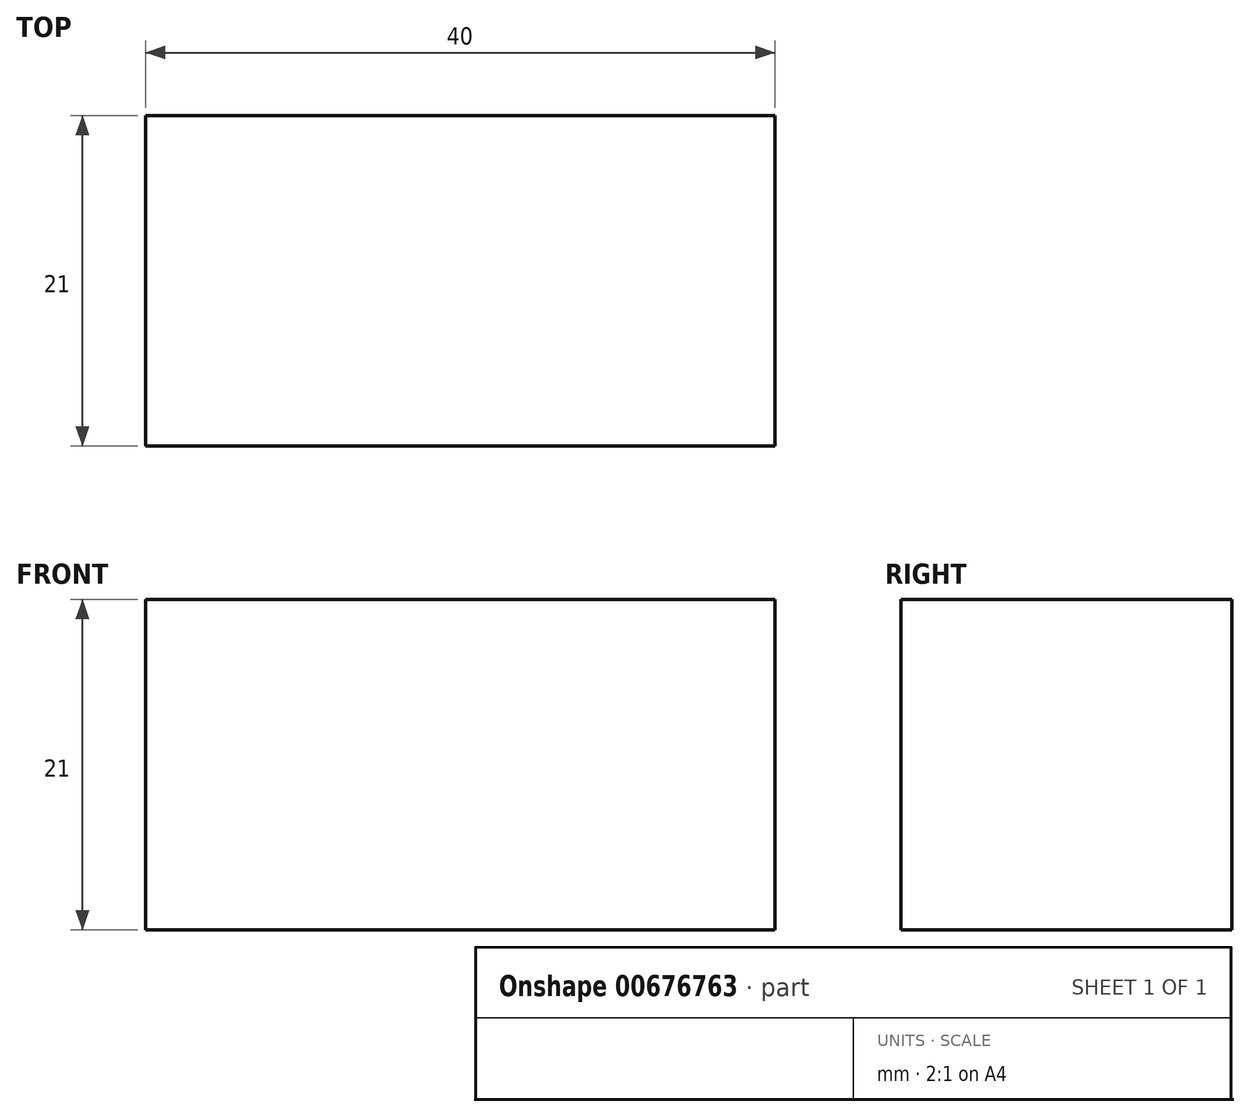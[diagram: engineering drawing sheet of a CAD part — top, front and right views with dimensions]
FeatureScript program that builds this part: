
annotation { "Feature Type Name" : "Feature", "Feature Type Description" : "" }
export const myFeature = defineFeature(function(context is Context, id is Id, definition is map)
    precondition{}
    {
        {
            var Q0;
            Q0=qCreatedBy(makeId("Right.planeOp"),FACE);
            var sketch = newSketch(context, id + "F0", { "sketchPlane" : qUnion([Q0])});
            skLineSegment(sketch, "E0.bottom", {"start": v(10.5, -10.5) * mm, "end": v(-10.5, -10.5) * mm});
            skLineSegment(sketch, "E0.top", {"start": v(10.5, 10.5) * mm, "end": v(-10.5, 10.5) * mm});
            skLineSegment(sketch, "E0.left", {"start": v(10.5, -10.5) * mm, "end": v(10.5, 10.5) * mm});
            skLineSegment(sketch, "E0.right", {"start": v(-10.5, -10.5) * mm, "end": v(-10.5, 10.5) * mm});
            skPoint(sketch, "E0.middle", {"position": v(0, 0) * mm});
            skSolve(sketch);
        }
        {
            var Q0;
            Q0=makeQuery(id+"F0.imprint","IMPRINT",FACE,{"disambiguationData":[TD([[makeQuery(id+"F0.imprint","IMPRINT",EDGE,{"derivedFrom":sQuery(id+"F0.wireOp",EDGE,"E0.bottom")}),-1.0]])]});
            extrude(context, id + "F1", {"entities" : qUnion([Q0]), "depth" : 40 * mm, "offsetDistance" : 25.4 * mm});
        }
    });
